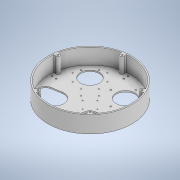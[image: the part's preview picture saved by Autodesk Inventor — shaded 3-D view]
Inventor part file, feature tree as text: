
AUTODESK INVENTOR PART (.ipt)
format: ipt  version: 2022 (Build 260153000, 153)  size: 333,312 bytes
history: native  units: mm
features: sketch x11, extrude x10, pattern_circular x1
ambient origin geometry x8: Origin, YZ Plane, XZ Plane, XY Plane, X Axis, Y Axis, Z Axis, Center Point
bodies: Solid1 (feature_tree)
feature tree (22):
  extrude  "Extrusion1"  Depth=40.0mm TaperAngle=0.0deg
  extrude  "Extrusion3"  Depth=37.0mm TaperAngle=0.0deg
  extrude  "Extrusion6"  Depth=42.0mm
  extrude  "Extrusion9"  Depth=42.0mm
  extrude  "Extrusion12"  TaperAngle=135.0deg  [1 undecoded]
  extrude  "Extrusion13"  Depth=24.0mm
  extrude  "Extrusion14"  Depth=3.5mm
  extrude  "Extrusion16"  Depth=3.5mm
  pattern_circular  "Circular Pattern4"  [2 undecoded]
  extrude  "Extrusion18"  Depth=10.0mm
  extrude  "Extrusion19"  TaperAngle=135.0deg  [1 undecoded]
  sketch  "Sketch1"  dims[d0=200.0mm d1=40.0mm d2=0.0mm]
  sketch  "Sketch3"  dims[d14=3.0mm d15=37.0mm d16=0.0mm]
  sketch  "Sketch6"  dims[d40=36.0mm d41=0.0mm d77=42.0mm]
  sketch  "Sketch9"  dims[d78=48.0mm d79=42.0mm]
  sketch  "Sketch12"  dims[d80=48.0mm d81=135.0deg]
  sketch  "Sketch13"  dims[d82=24.0mm d83=24.0mm]
  sketch  "Sketch14"  dims[d84=24.0mm d85=3.5mm]
  sketch  "Sketch16"  dims[d86=3.5mm d87=3.5mm]
  sketch  "Sketch17"  dims[d88=3.5mm]
  sketch  "Sketch18"  dims[d89=35.0mm]
  sketch  "Sketch20"  dims[d90=4.0mm d91=0.0mm d106=4.4mm d109=92.0mm d111=135.0deg d112=10.0mm d113=50.0mm d115=360.0deg d132=135.0deg d133=58.5mm d134=26.0mm d135=48.0mm d136=10.0mm d137=0.0mm d138=2.3mm d139=2.3mm d140=2.3mm d141=2.3mm d142=25.0mm d143=25.0mm d146=7.0mm d147=2.3mm d148=2.3mm d149=2.3mm d150=2.3mm d151=10.0mm d152=0.0mm d153=20.0mm d154=30.0mm d155=2.3mm d156=2.3mm d157=2.3mm d158=2.3mm d160=7.0mm d165=10.0mm d166=0.0mm d179=3.5mm d180=19.5mm d181=9.5mm d182=3.5mm d183=10.0mm d184=0.0mm d185=40.0mm d186=360.0deg d188=45.0deg d189=75.0mm d190=20.0mm d191=20.0mm d193=45.0deg d194=2.3mm d195=2.3mm d196=2.3mm d197=2.3mm d198=48.0mm d199=26.0mm d200=58.5mm d201=47.0mm d202=10.5mm d203=65.0mm d204=32.5mm d205=10.0mm d206=0.0mm d207=60.0mm d208=45.0mm d209=45.0deg d210=40.0mm d212=360.0deg d214=10.0mm d215=0.0mm d216=15.0mm d217=225.0deg d218=225.0deg d219=47.0mm d220=65.0mm d221=32.5mm d222=10.5mm d223=135.0deg d224=3.5mm d225=3.5mm d226=20.0mm d227=32.0mm d228=30.0mm d229=3.5mm d230=3.5mm d231=50.0mm d232=10.0mm d233=0.0mm]
note: 4 required parameter values undecoded (feature->parameter linkage not recoverable at this tier; creation-order binding heuristic only, values carry confidence <= 0.55)
